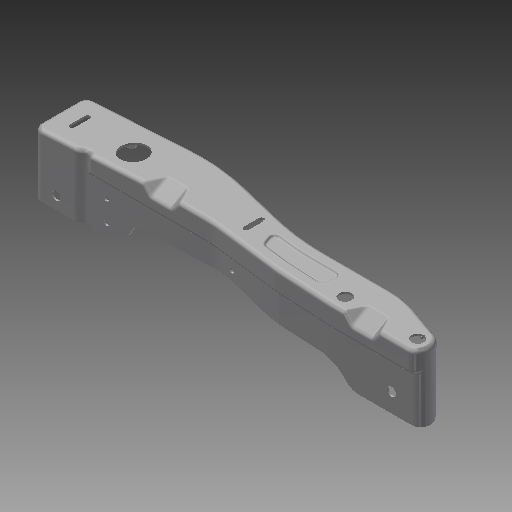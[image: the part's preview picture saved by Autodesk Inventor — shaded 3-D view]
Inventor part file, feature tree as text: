
AUTODESK INVENTOR PART (.ipt)
format: ipt  version: 2019 (Build 230136000, 136)  size: 1,150,464 bytes
history: native  units: mm
features: other x2, plane x1
ambient origin geometry x8: Origin, YZ Plane, XZ Plane, XY Plane, X Axis, Y Axis, Z Axis, Center Point
bodies: Solid1 (feature_tree)
feature tree (3):
  other  "Top Frame Right Plate.ipt"
  plane  "Work Plane1"
  other  "Solid1::Top Frame Right Plate.ipt"
